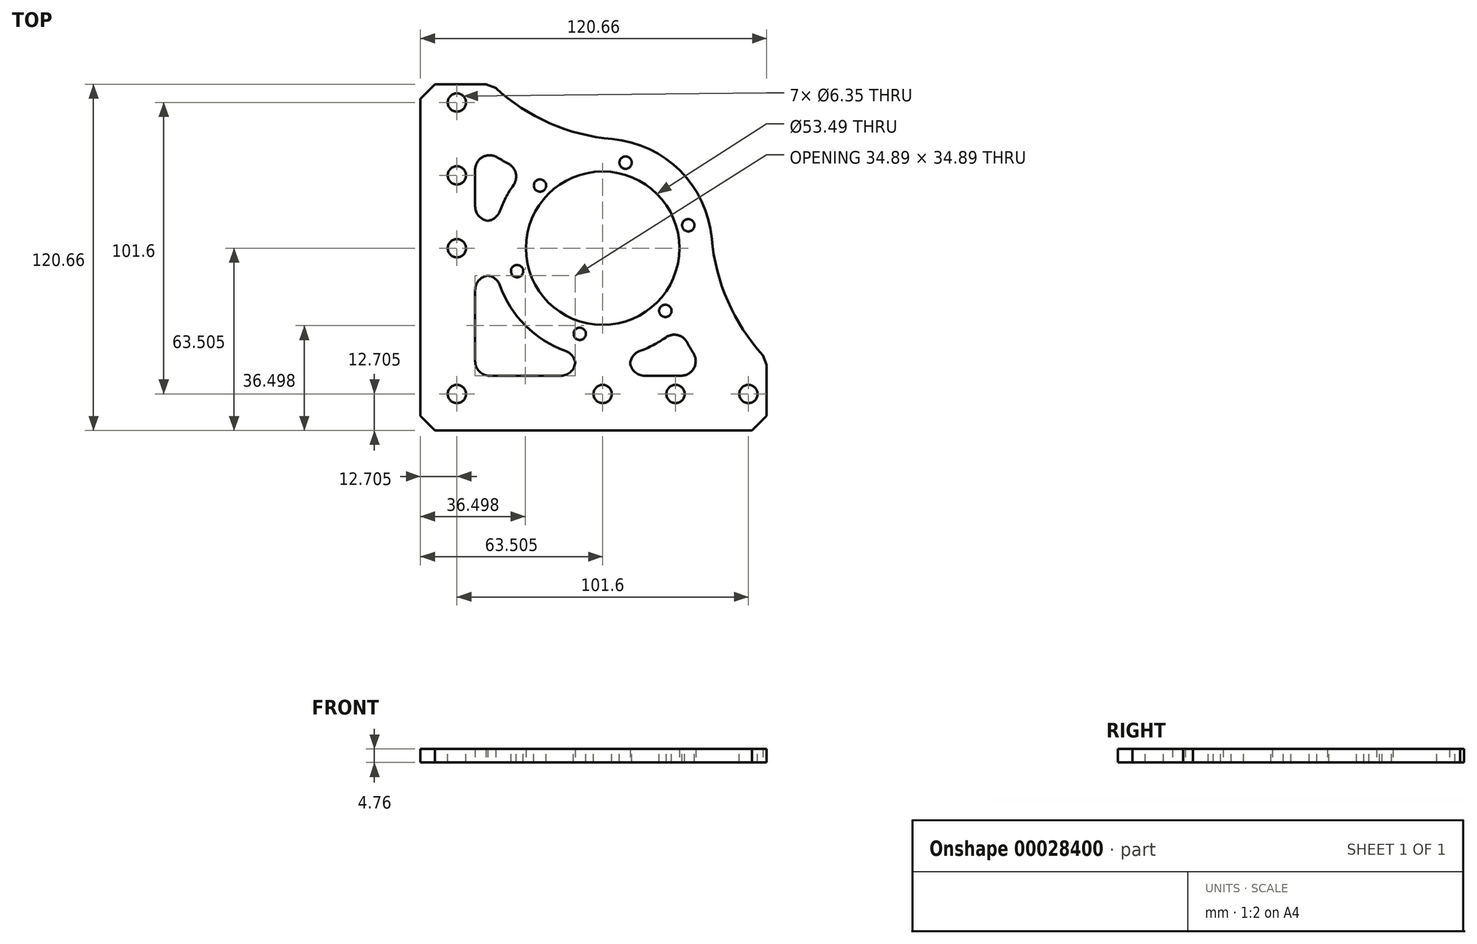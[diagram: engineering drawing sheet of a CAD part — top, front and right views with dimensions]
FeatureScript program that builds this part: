
annotation { "Feature Type Name" : "Feature", "Feature Type Description" : "" }
export const myFeature = defineFeature(function(context is Context, id is Id, definition is map)
    precondition{}
    {
        {
            var Q0;
            Q0=qCreatedBy(makeId("Top.planeOp"),FACE);
            var sketch = newSketch(context, id + "F0", { "sketchPlane" : qUnion([Q0])});
            skLineSegment(sketch, "E0.rect.bottom", {"start": v(-60.32, 60.32) * mm, "end": v(-35.54, 60.32) * mm});
            skLineSegment(sketch, "E0.rect.top", {"start": v(-60.33, -60.33) * mm, "end": v(60.32, -60.33) * mm});
            skLineSegment(sketch, "E0.rect.left", {"start": v(-60.33, 60.32) * mm, "end": v(-60.33, -60.32) * mm});
            skLineSegment(sketch, "E0.rect.right", {"start": v(60.32, 60.33) * mm, "end": v(60.32, 60.31) * mm});
            skPoint(sketch, "E0.rect.middle", {"position": v(0, 0) * mm});
            skCircle(sketch, "E1", {"center": v(3.17, 3.17) * mm, "radius": 26.75 * mm});
            skArc(sketch, "E2", {"start": v(41.2, 6.46) * mm, "mid": v(30.17, 30.17) * mm, "end": v(6.46, 41.2) * mm});
            skArc(sketch, "E3", {"start": v(-35.54, 60.32) * mm, "mid": v(-16.18, 47.15) * mm, "end": v(6.46, 41.2) * mm});
            skArc(sketch, "E4", {"start": v(61.15, 61.15) * mm, "mid": v(60.74, 60.73) * mm, "end": v(60.32, 60.31) * mm});
            skArc(sketch, "E5.trimOffspring", {"start": v(60.31, 60.33) * mm, "mid": v(60.73, 60.74) * mm, "end": v(61.15, 61.15) * mm});
            skArc(sketch, "E6.trimOffspring", {"start": v(41.2, 6.46) * mm, "mid": v(47.15, -16.18) * mm, "end": v(60.32, -35.54) * mm});
            skLineSegment(sketch, "E7.trimOffspring", {"start": v(60.31, 60.33) * mm, "end": v(60.33, 60.33) * mm});
            skLineSegment(sketch, "E8.trimOffspring", {"start": v(60.32, -35.54) * mm, "end": v(60.32, -60.32) * mm});
            skArc(sketch, "E9.0", {"start": v(-41.28, 40.16) * mm, "mid": v(-32.97, 34.5) * mm, "end": v(-24.07, 29.8) * mm});
            skArc(sketch, "E10.0", {"start": v(29.8, -24.07) * mm, "mid": v(34.5, -32.97) * mm, "end": v(40.16, -41.27) * mm});
            skArc(sketch, "E11", {"start": v(-33.72, -6.35) * mm, "mid": v(-23.77, -23.77) * mm, "end": v(-6.35, -33.72) * mm});
            skLineSegment(sketch, "E12", {"start": v(-41.28, 40.16) * mm, "end": v(-41.28, 12.7) * mm});
            skLineSegment(sketch, "E13", {"start": v(40.16, -41.27) * mm, "end": v(12.7, -41.27) * mm});
            skLineSegment(sketch, "E14", {"start": v(3.17, 3.17) * mm, "end": v(-80.6, 3.17) * mm, "construction": true});
            skLineSegment(sketch, "E15", {"start": v(3.17, 3.17) * mm, "end": v(3.17, -69.39) * mm, "construction": true});
            skLineSegment(sketch, "E16", {"start": v(-33.72, 12.7) * mm, "end": v(-41.28, 12.7) * mm});
            skLineSegment(sketch, "E17", {"start": v(-33.72, -6.35) * mm, "end": v(-41.27, -6.35) * mm});
            skLineSegment(sketch, "E18", {"start": v(-6.35, -33.72) * mm, "end": v(-6.35, -41.28) * mm});
            skLineSegment(sketch, "E19", {"start": v(12.7, -33.72) * mm, "end": v(12.7, -41.27) * mm});
            skLineSegment(sketch, "E20.trimOffspring", {"start": v(-41.28, -6.35) * mm, "end": v(-41.28, -41.27) * mm});
            skLineSegment(sketch, "E21.trimOffspring", {"start": v(-6.35, -41.27) * mm, "end": v(-41.28, -41.27) * mm});
            skArc(sketch, "E22.trimOffspring", {"start": v(12.7, -33.72) * mm, "mid": v(21.89, -30.01) * mm, "end": v(29.8, -24.07) * mm});
            skArc(sketch, "E23.trimOffspring", {"start": v(-24.07, 29.8) * mm, "mid": v(-30.01, 21.89) * mm, "end": v(-33.72, 12.7) * mm});
            skSolve(sketch);
        }
        {
            var Q0;
            {var subQ4=sQuery(id+"F0.wireOp",EDGE,"E0.rect.top");Q0=makeQuery(id+"F0.imprint","IMPRINT",FACE,{"disambiguationData":[TD([[makeQuery(id+"F0.imprint","IMPRINT",EDGE,{"derivedFrom":subQ4}),1.0]])]});}
            var Q1;
            Q1=makeQuery(id+"F0.imprint","IMPRINT",FACE,{"disambiguationData":[TD([[makeQuery(id+"F0.imprint","IMPRINT",EDGE,{"derivedFrom":sQuery(id+"F0.wireOp",EDGE,"E1")}),-1.0]])]});
            extrude(context, id + "F1", {"entities" : qUnion([Q0, Q1]), "depth" : 4.76 * mm});
        }
        {
            var Q0;
            Q0=makeQuery(id+"F1.opExtrude","CAP_FACE",FACE,{"disambiguationData":[OSD([sQuery(id+"F0.wireOp",EDGE,"E0.rect.bottom"),sQuery(id+"F0.wireOp",EDGE,"E0.rect.top"),sQuery(id+"F0.wireOp",EDGE,"E0.rect.left"),sQuery(id+"F0.wireOp",EDGE,"E0.rect.right"),sQuery(id+"F0.wireOp",EDGE,"E1"),sQuery(id+"F0.wireOp",EDGE,"E2"),sQuery(id+"F0.wireOp",EDGE,"E3"),sQuery(id+"F0.wireOp",EDGE,"E6.trimOffspring")])],"isStart":false});
            var sketch = newSketch(context, id + "F2", { "sketchPlane" : qUnion([Q0])});
            skCircle(sketch, "E24.cCircle", {"center": v(3.17, 3.17) * mm, "radius": 30.88 * mm, "construction": true});
            skLineSegment(sketch, "E24.0", {"start": v(-4.82, -26.66) * mm, "end": v(-26.66, -4.82) * mm});
            skLineSegment(sketch, "E24.1", {"start": v(-26.66, -4.82) * mm, "end": v(-18.66, 25.01) * mm});
            skLineSegment(sketch, "E24.2", {"start": v(-18.66, 25.01) * mm, "end": v(11.17, 33) * mm});
            skLineSegment(sketch, "E24.3", {"start": v(11.17, 33) * mm, "end": v(33, 11.17) * mm});
            skLineSegment(sketch, "E24.4", {"start": v(33, 11.17) * mm, "end": v(25.01, -18.66) * mm});
            skLineSegment(sketch, "E24.5", {"start": v(25.01, -18.66) * mm, "end": v(-4.82, -26.66) * mm});
            skLineSegment(sketch, "E25", {"start": v(-47.62, -47.62) * mm, "end": v(53.98, -47.62) * mm});
            skLineSegment(sketch, "E26", {"start": v(-47.62, -47.62) * mm, "end": v(-47.63, 53.98) * mm});
            skPoint(sketch, "E27", {"position": v(-47.63, 28.58) * mm});
            skPoint(sketch, "E28", {"position": v(-47.63, 3.18) * mm});
            skPoint(sketch, "E29", {"position": v(28.58, -47.62) * mm});
            skPoint(sketch, "E30", {"position": v(3.18, -47.62) * mm});
            skLineSegment(sketch, "E31", {"start": v(3.18, 3.17) * mm, "end": v(36.55, 36.55) * mm, "construction": true});
            skPoint(sketch, "E32", {"position": v(22.09, 22.09) * mm});
            skSolve(sketch);
        }
        {
            var Q0;
            Q0=sQuery(id+"F2.wireOp",VERTEX,"E24.2.start");
            var Q1;
            Q1=sQuery(id+"F2.wireOp",VERTEX,"E24.3.start");
            var Q2;
            Q2=sQuery(id+"F2.wireOp",VERTEX,"E24.4.start");
            var Q3;
            Q3=sQuery(id+"F2.wireOp",VERTEX,"E24.5.start");
            var Q4;
            Q4=sQuery(id+"F2.wireOp",VERTEX,"E24.0.start");
            var Q5;
            Q5=sQuery(id+"F2.wireOp",VERTEX,"E24.1.start");
            var Q6;
            Q6=makeQuery(id+"F1.opExtrude","SWEPT_BODY",BODY,{"disambiguationData":[OSD([sQuery(id+"F0.wireOp",EDGE,"E0.rect.bottom"),sQuery(id+"F0.wireOp",EDGE,"E0.rect.top"),sQuery(id+"F0.wireOp",EDGE,"E0.rect.left"),sQuery(id+"F0.wireOp",EDGE,"E0.rect.right"),sQuery(id+"F0.wireOp",EDGE,"E1"),sQuery(id+"F0.wireOp",EDGE,"E2"),sQuery(id+"F0.wireOp",EDGE,"E3"),sQuery(id+"F0.wireOp",EDGE,"E6.trimOffspring")])]});
            hole(context, id + "F3", {"style" : HoleStyle.SIMPLE, "holeDiameter" : 4.3 * mm, "endStyle" : HoleEndStyle.THROUGH, "locations" : qUnion([Q0, Q1, Q2, Q3, Q4, Q5]), "scope" : qUnion([Q6])});
        }
        {
            var Q0;
            Q0=sQuery(id+"F2.wireOp",VERTEX,"E26.end");
            var Q1;
            Q1=sQuery(id+"F2.wireOp",VERTEX,"E27");
            var Q2;
            Q2=sQuery(id+"F2.wireOp",VERTEX,"E28");
            var Q3;
            Q3=sQuery(id+"F2.wireOp",VERTEX,"E26.start");
            var Q4;
            Q4=sQuery(id+"F2.wireOp",VERTEX,"E30");
            var Q5;
            Q5=sQuery(id+"F2.wireOp",VERTEX,"E29");
            var Q6;
            Q6=sQuery(id+"F2.wireOp",VERTEX,"E25.end");
            var Q7;
            Q7=makeQuery(id+"F1.opExtrude","SWEPT_BODY",BODY,{"disambiguationData":[OSD([sQuery(id+"F0.wireOp",EDGE,"E0.rect.bottom"),sQuery(id+"F0.wireOp",EDGE,"E0.rect.top"),sQuery(id+"F0.wireOp",EDGE,"E0.rect.left"),sQuery(id+"F0.wireOp",EDGE,"E0.rect.right"),sQuery(id+"F0.wireOp",EDGE,"E1"),sQuery(id+"F0.wireOp",EDGE,"E2"),sQuery(id+"F0.wireOp",EDGE,"E3"),sQuery(id+"F0.wireOp",EDGE,"E6.trimOffspring")])]});
            hole(context, id + "F4", {"style" : HoleStyle.SIMPLE, "holeDiameter" : 6.35 * mm, "endStyle" : HoleEndStyle.THROUGH, "locations" : qUnion([Q0, Q1, Q2, Q3, Q4, Q5, Q6]), "scope" : qUnion([Q7])});
        }
        {
            var Q0;
            Q0=makeQuery(id+"F1.opExtrude","SWEPT_EDGE",EDGE,{"disambiguationData":[OSD([sQuery(id+"F0.wireOp",EDGE,"E9.0"),sQuery(id+"F0.wireOp",EDGE,"E12")])]});
            var Q1;
            Q1=makeQuery(id+"F1.opExtrude","SWEPT_EDGE",EDGE,{"disambiguationData":[OSD([sQuery(id+"F0.wireOp",EDGE,"E9.0"),sQuery(id+"F0.wireOp",EDGE,"E23.trimOffspring")])]});
            var Q2;
            Q2=makeQuery(id+"F1.opExtrude","SWEPT_EDGE",EDGE,{"disambiguationData":[OSD([sQuery(id+"F0.wireOp",EDGE,"E16"),sQuery(id+"F0.wireOp",EDGE,"E23.trimOffspring")])]});
            var Q3;
            Q3=makeQuery(id+"F1.opExtrude","SWEPT_EDGE",EDGE,{"disambiguationData":[OSD([sQuery(id+"F0.wireOp",EDGE,"E12"),sQuery(id+"F0.wireOp",EDGE,"E16")])]});
            var Q4;
            Q4=makeQuery(id+"F1.opExtrude","SWEPT_EDGE",EDGE,{"disambiguationData":[OSD([sQuery(id+"F0.wireOp",EDGE,"E11"),sQuery(id+"F0.wireOp",EDGE,"E17")])]});
            var Q5;
            Q5=makeQuery(id+"F1.opExtrude","SWEPT_EDGE",EDGE,{"disambiguationData":[OSD([sQuery(id+"F0.wireOp",EDGE,"E17"),sQuery(id+"F0.wireOp",EDGE,"E20.trimOffspring")])]});
            var Q6;
            Q6=makeQuery(id+"F1.opExtrude","SWEPT_EDGE",EDGE,{"disambiguationData":[OSD([sQuery(id+"F0.wireOp",EDGE,"E11"),sQuery(id+"F0.wireOp",EDGE,"E18")])]});
            var Q7;
            Q7=makeQuery(id+"F1.opExtrude","SWEPT_EDGE",EDGE,{"disambiguationData":[OSD([sQuery(id+"F0.wireOp",EDGE,"E20.trimOffspring"),sQuery(id+"F0.wireOp",EDGE,"E21.trimOffspring")])]});
            var Q8;
            Q8=makeQuery(id+"F1.opExtrude","SWEPT_EDGE",EDGE,{"disambiguationData":[OSD([sQuery(id+"F0.wireOp",EDGE,"E18"),sQuery(id+"F0.wireOp",EDGE,"E21.trimOffspring")])]});
            var Q9;
            Q9=makeQuery(id+"F1.opExtrude","SWEPT_EDGE",EDGE,{"disambiguationData":[OSD([sQuery(id+"F0.wireOp",EDGE,"E10.0"),sQuery(id+"F0.wireOp",EDGE,"E13")])]});
            var Q10;
            Q10=makeQuery(id+"F1.opExtrude","SWEPT_EDGE",EDGE,{"disambiguationData":[OSD([sQuery(id+"F0.wireOp",EDGE,"E10.0"),sQuery(id+"F0.wireOp",EDGE,"E22.trimOffspring")])]});
            var Q11;
            Q11=makeQuery(id+"F1.opExtrude","SWEPT_EDGE",EDGE,{"disambiguationData":[OSD([sQuery(id+"F0.wireOp",EDGE,"E19"),sQuery(id+"F0.wireOp",EDGE,"E22.trimOffspring")])]});
            var Q12;
            Q12=makeQuery(id+"F1.opExtrude","SWEPT_EDGE",EDGE,{"disambiguationData":[OSD([sQuery(id+"F0.wireOp",EDGE,"E13"),sQuery(id+"F0.wireOp",EDGE,"E19")])]});
            fillet(context, id + "F5", {"entities" : qUnion([Q0, Q1, Q2, Q3, Q4, Q5, Q6, Q7, Q8, Q9, Q10, Q11, Q12]), "radius" : 5.08 * mm, "tangentPropagation" : true, "allowEdgeOverflow" : false});
        }
        {
            var Q0;
            Q0=makeQuery(id+"F1.opExtrude","SWEPT_EDGE",EDGE,{"disambiguationData":[OSD([sQuery(id+"F0.wireOp",EDGE,"E0.rect.top"),sQuery(id+"F0.wireOp",EDGE,"E0.rect.left")])]});
            var Q1;
            Q1=makeQuery(id+"F1.opExtrude","SWEPT_EDGE",EDGE,{"disambiguationData":[OSD([sQuery(id+"F0.wireOp",EDGE,"E0.rect.top"),sQuery(id+"F0.wireOp",EDGE,"E8.trimOffspring")])]});
            var Q2;
            Q2=makeQuery(id+"F1.opExtrude","SWEPT_EDGE",EDGE,{"disambiguationData":[OSD([sQuery(id+"F0.wireOp",EDGE,"E6.trimOffspring"),sQuery(id+"F0.wireOp",EDGE,"E8.trimOffspring")])]});
            var Q3;
            Q3=makeQuery(id+"F1.opExtrude","SWEPT_EDGE",EDGE,{"disambiguationData":[OSD([sQuery(id+"F0.wireOp",EDGE,"E0.rect.bottom"),sQuery(id+"F0.wireOp",EDGE,"E3")])]});
            var Q4;
            Q4=makeQuery(id+"F1.opExtrude","SWEPT_EDGE",EDGE,{"disambiguationData":[OSD([sQuery(id+"F0.wireOp",EDGE,"E0.rect.bottom"),sQuery(id+"F0.wireOp",EDGE,"E0.rect.left")])]});
            chamfer(context, id + "F6", {"entities" : qUnion([Q0, Q1, Q2, Q3, Q4]), "width" : 5.08 * mm, "tangentPropagation" : true});
        }
    });
